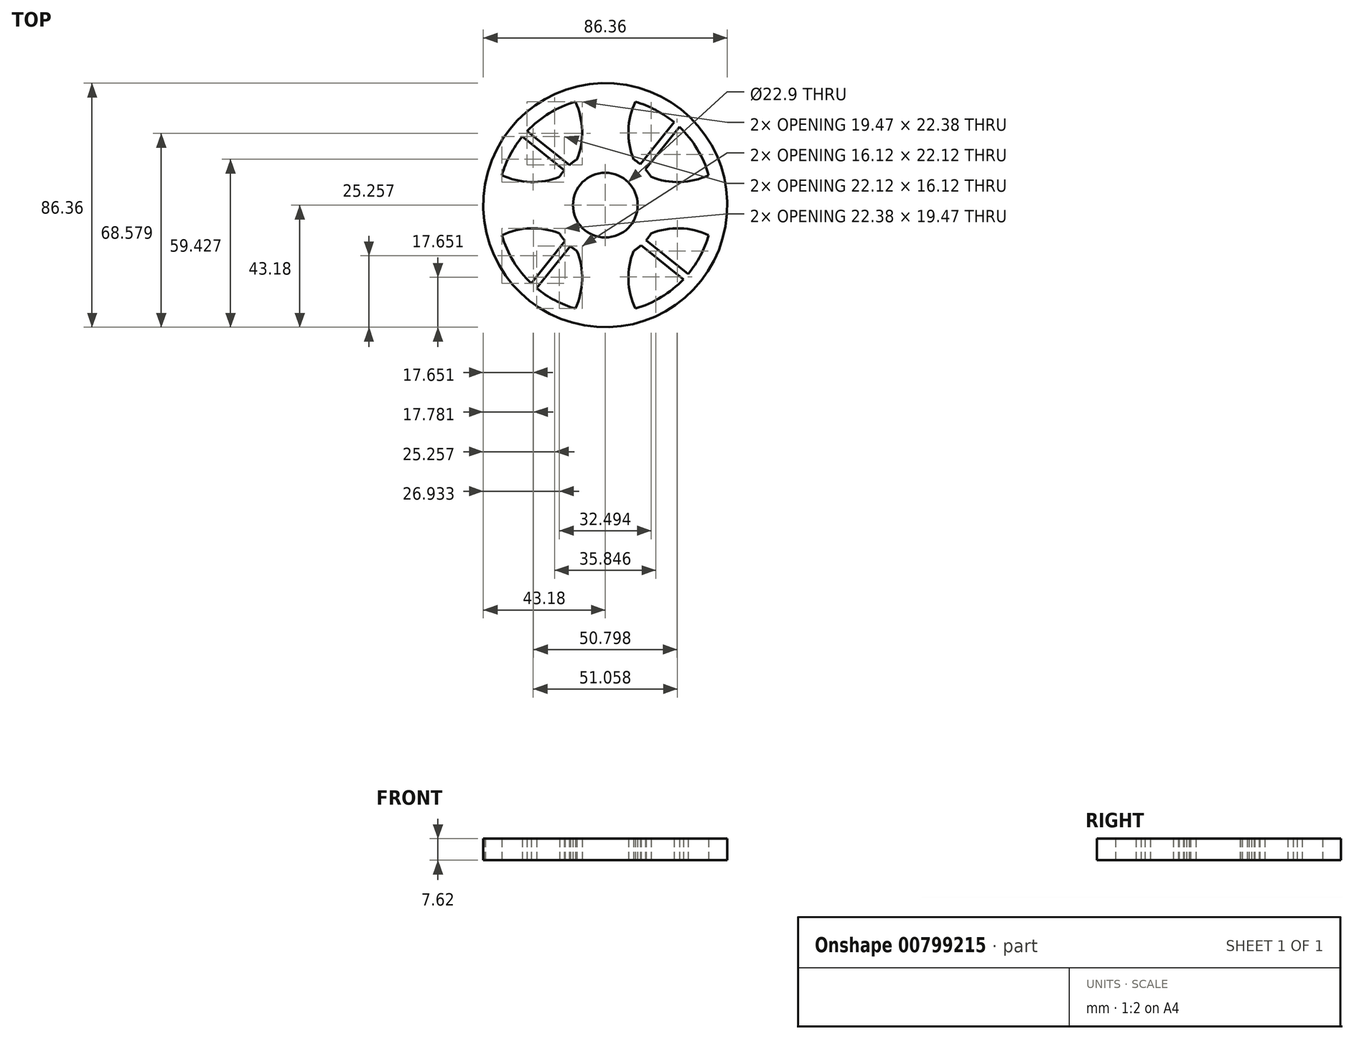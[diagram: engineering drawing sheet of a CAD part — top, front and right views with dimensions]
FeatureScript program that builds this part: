
annotation { "Feature Type Name" : "Feature", "Feature Type Description" : "" }
export const myFeature = defineFeature(function(context is Context, id is Id, definition is map)
    precondition{}
    {
        {
            var Q0;
            Q0=qCreatedBy(makeId("Top.planeOp"),FACE);
            var sketch = newSketch(context, id + "F0", { "sketchPlane" : qUnion([Q0])});
            skCircle(sketch, "E0", {"center": v(0, 0) * mm, "radius": 11.45 * mm});
            skCircle(sketch, "E1", {"center": v(0, 0) * mm, "radius": 19.05 * mm});
            skArc(sketch, "E2", {"start": v(-10.04, 16.2) * mm, "mid": v(-8.22, 27.23) * mm, "end": v(-11.33, 37.98) * mm});
            skArc(sketch, "E3.MirrorCS", {"start": v(10.04, 16.2) * mm, "mid": v(8.22, 27.23) * mm, "end": v(11.33, 37.98) * mm});
            skCircle(sketch, "E4", {"center": v(0, 0) * mm, "radius": 38.1 * mm});
            skCircle(sketch, "E5", {"center": v(0, 0) * mm, "radius": 43.18 * mm});
            skArc(sketch, "E6", {"start": v(0, 44.45) * mm, "mid": v(-6.68, 43) * mm, "end": v(-11.33, 37.98) * mm});
            skArc(sketch, "E7", {"start": v(11.33, 37.98) * mm, "mid": v(6.68, 43) * mm, "end": v(0, 44.45) * mm});
            skArc(sketch, "E8.1.1", {"start": v(-38.2, 11.02) * mm, "mid": v(-43.22, 6.37) * mm, "end": v(-44.68, -0.3) * mm});
            skArc(sketch, "E8.1.4", {"start": v(-44.45, 0) * mm, "mid": v(-43, -6.68) * mm, "end": v(-37.98, -11.33) * mm});
            skArc(sketch, "E8.1.6", {"start": v(-16.2, -10.04) * mm, "mid": v(-27.23, -8.22) * mm, "end": v(-37.98, -11.33) * mm});
            skArc(sketch, "E8.2.1", {"start": v(-11.33, -37.98) * mm, "mid": v(-6.68, -43) * mm, "end": v(0, -44.45) * mm});
            skArc(sketch, "E8.2.2", {"start": v(-10.04, -16.2) * mm, "mid": v(-8.22, -27.23) * mm, "end": v(-11.33, -37.98) * mm});
            skArc(sketch, "E8.2.4", {"start": v(0, -44.45) * mm, "mid": v(6.68, -43) * mm, "end": v(11.33, -37.98) * mm});
            skArc(sketch, "E8.2.6", {"start": v(10.04, -16.2) * mm, "mid": v(8.22, -27.23) * mm, "end": v(11.33, -37.98) * mm});
            skArc(sketch, "E8.3.1", {"start": v(37.98, -11.33) * mm, "mid": v(43, -6.68) * mm, "end": v(44.45, 0) * mm});
            skArc(sketch, "E8.3.2", {"start": v(16.2, -10.04) * mm, "mid": v(27.23, -8.22) * mm, "end": v(37.98, -11.33) * mm});
            skArc(sketch, "E8.3.4", {"start": v(44.45, 0) * mm, "mid": v(43, 6.68) * mm, "end": v(37.98, 11.33) * mm});
            skArc(sketch, "E8.3.6", {"start": v(16.2, 10.04) * mm, "mid": v(27.23, 8.22) * mm, "end": v(37.98, 11.33) * mm});
            skLineSegment(sketch, "E9", {"start": v(-14.47, 12.4) * mm, "end": v(-29.34, 24.3) * mm});
            skLineSegment(sketch, "E10", {"start": v(-12.69, 14.2) * mm, "end": v(-27.66, 26.2) * mm});
            skLineSegment(sketch, "E11.1.0", {"start": v(-12.4, -14.47) * mm, "end": v(-24.3, -29.34) * mm});
            skLineSegment(sketch, "E11.1.1", {"start": v(-14.2, -12.69) * mm, "end": v(-26.2, -27.66) * mm});
            skLineSegment(sketch, "E11.2.0", {"start": v(14.47, -12.4) * mm, "end": v(29.34, -24.3) * mm});
            skLineSegment(sketch, "E11.2.1", {"start": v(12.69, -14.2) * mm, "end": v(27.66, -26.2) * mm});
            skLineSegment(sketch, "E11.3.0", {"start": v(12.4, 14.47) * mm, "end": v(24.3, 29.34) * mm});
            skLineSegment(sketch, "E11.3.1", {"start": v(14.2, 12.69) * mm, "end": v(26.2, 27.66) * mm});
            skArc(sketch, "E12.MirrorCS", {"start": v(-16.2, 10.04) * mm, "mid": v(-27.23, 8.22) * mm, "end": v(-37.98, 11.33) * mm});
            skArc(sketch, "E13.MirrorCS", {"start": v(-44.45, 0) * mm, "mid": v(-43, 6.68) * mm, "end": v(-37.98, 11.33) * mm});
            skSolve(sketch);
        }
        {
            var Q0;
            {var subQ0=sQuery(id+"F0.wireOp",EDGE,"E2");var subQ1=sQuery(id+"F0.wireOp",EDGE,"E1");var subQ2=makeQuery(id+"F0.imprint","INTERSECT",VERTEX,{"derivedFrom":[subQ1,subQ0]});Q0=makeQuery(id+"F0.imprint","IMPRINT",FACE,{"disambiguationData":[TD([[makeQuery(id+"F0.imprint","IMPRINT",EDGE,{"disambiguationData":[TD([[subQ2,1.0]])],"derivedFrom":subQ1}),-1.0]])]});}
            var Q1;
            Q1=makeQuery(id+"F0.imprint","IMPRINT",FACE,{"disambiguationData":[TD([[makeQuery(id+"F0.imprint","IMPRINT",EDGE,{"derivedFrom":sQuery(id+"F0.wireOp",EDGE,"E0")}),-1.0]])]});
            var Q2;
            {var subQ1=sQuery(id+"F0.wireOp",EDGE,"E2");var subQ5=sQuery(id+"F0.wireOp",EDGE,"E6");var subQ6=makeQuery(id+"F0.imprint","INTERSECT",VERTEX,{"derivedFrom":[subQ1,subQ5]});Q2=makeQuery(id+"F0.imprint","IMPRINT",FACE,{"disambiguationData":[TD([[makeQuery(id+"F0.imprint","IMPRINT",EDGE,{"disambiguationData":[TD([[subQ6,1.0]])],"derivedFrom":subQ1}),-1.0]])]});}
            var Q3;
            {var subQ9=sQuery(id+"F0.wireOp",EDGE,"E2");var subQ11=sQuery(id+"F0.wireOp",EDGE,"E6");var subQ12=makeQuery(id+"F0.imprint","INTERSECT",VERTEX,{"derivedFrom":[subQ9,subQ11]});Q3=makeQuery(id+"F0.imprint","IMPRINT",FACE,{"disambiguationData":[TD([[makeQuery(id+"F0.imprint","IMPRINT",EDGE,{"disambiguationData":[TD([[subQ12,1.0]])],"derivedFrom":subQ9}),1.0]])]});}
            var Q4;
            {var subQ0=sQuery(id+"F0.wireOp",EDGE,"E8.1.2");var subQ5=sQuery(id+"F0.wireOp",EDGE,"E4");var subQ6=makeQuery(id+"F0.imprint","INTERSECT",VERTEX,{"derivedFrom":[subQ5,subQ0]});Q4=makeQuery(id+"F0.imprint","IMPRINT",FACE,{"disambiguationData":[TD([[makeQuery(id+"F0.imprint","IMPRINT",EDGE,{"disambiguationData":[TD([[subQ6,-1.0]])],"derivedFrom":subQ5}),-1.0]])]});}
            var Q5;
            {var subQ5=sQuery(id+"F0.wireOp",EDGE,"E4");var subQ7=makeQuery(id+"F0.imprint","INTERSECT",VERTEX,{"derivedFrom":[subQ5,sQuery(id+"F0.wireOp",EDGE,"E11.1.1")]});Q5=makeQuery(id+"F0.imprint","IMPRINT",FACE,{"disambiguationData":[TD([[makeQuery(id+"F0.imprint","IMPRINT",EDGE,{"disambiguationData":[TD([[subQ7,1.0]])],"derivedFrom":subQ5}),-1.0]])]});}
            var Q6;
            {var subQ0=sQuery(id+"F0.wireOp",EDGE,"E11.1.0");Q6=makeQuery(id+"F0.imprint","IMPRINT",FACE,{"disambiguationData":[TD([[makeQuery(id+"F0.imprint","IMPRINT",EDGE,{"derivedFrom":subQ0}),-1.0]])]});}
            var Q7;
            {var subQ0=sQuery(id+"F0.wireOp",EDGE,"E8.2.2");var subQ1=sQuery(id+"F0.wireOp",EDGE,"E1");var subQ2=makeQuery(id+"F0.imprint","INTERSECT",VERTEX,{"derivedFrom":[subQ1,subQ0]});Q7=makeQuery(id+"F0.imprint","IMPRINT",FACE,{"disambiguationData":[TD([[makeQuery(id+"F0.imprint","IMPRINT",EDGE,{"disambiguationData":[TD([[subQ2,-1.0]])],"derivedFrom":subQ1}),-1.0]])]});}
            var Q8;
            {var subQ0=sQuery(id+"F0.wireOp",EDGE,"E8.2.2");var subQ5=sQuery(id+"F0.wireOp",EDGE,"E4");var subQ6=makeQuery(id+"F0.imprint","INTERSECT",VERTEX,{"derivedFrom":[subQ5,subQ0]});Q8=makeQuery(id+"F0.imprint","IMPRINT",FACE,{"disambiguationData":[TD([[makeQuery(id+"F0.imprint","IMPRINT",EDGE,{"disambiguationData":[TD([[subQ6,-1.0]])],"derivedFrom":subQ5}),-1.0]])]});}
            var Q9;
            {var subQ3=sQuery(id+"F0.wireOp",EDGE,"E4");var subQ9=sQuery(id+"F0.wireOp",EDGE,"E8.3.6");var subQ10=makeQuery(id+"F0.imprint","INTERSECT",VERTEX,{"derivedFrom":[subQ3,subQ9]});Q9=makeQuery(id+"F0.imprint","IMPRINT",FACE,{"disambiguationData":[TD([[makeQuery(id+"F0.imprint","IMPRINT",EDGE,{"disambiguationData":[TD([[subQ10,1.0]])],"derivedFrom":subQ3}),-1.0]])]});}
            var Q10;
            {var subQ0=sQuery(id+"F0.wireOp",EDGE,"E8.3.2");var subQ1=sQuery(id+"F0.wireOp",EDGE,"E1");var subQ2=makeQuery(id+"F0.imprint","INTERSECT",VERTEX,{"derivedFrom":[subQ1,subQ0]});Q10=makeQuery(id+"F0.imprint","IMPRINT",FACE,{"disambiguationData":[TD([[makeQuery(id+"F0.imprint","IMPRINT",EDGE,{"disambiguationData":[TD([[subQ2,-1.0]])],"derivedFrom":subQ1}),-1.0]])]});}
            var Q11;
            {var subQ0=sQuery(id+"F0.wireOp",EDGE,"E11.2.0");Q11=makeQuery(id+"F0.imprint","IMPRINT",FACE,{"disambiguationData":[TD([[makeQuery(id+"F0.imprint","IMPRINT",EDGE,{"derivedFrom":subQ0}),-1.0]])]});}
            var Q12;
            {var subQ0=sQuery(id+"F0.wireOp",EDGE,"E9");Q12=makeQuery(id+"F0.imprint","IMPRINT",FACE,{"disambiguationData":[TD([[makeQuery(id+"F0.imprint","IMPRINT",EDGE,{"derivedFrom":subQ0}),-1.0]])]});}
            var Q13;
            {var subQ0=sQuery(id+"F0.wireOp",EDGE,"E11.3.0");Q13=makeQuery(id+"F0.imprint","IMPRINT",FACE,{"disambiguationData":[TD([[makeQuery(id+"F0.imprint","IMPRINT",EDGE,{"derivedFrom":subQ0}),-1.0]])]});}
            var Q14;
            {var subQ0=sQuery(id+"F0.wireOp",EDGE,"E4");var subQ4=makeQuery(id+"F0.imprint","INTERSECT",VERTEX,{"derivedFrom":[subQ0,sQuery(id+"F0.wireOp",EDGE,"E11.2.1")]});Q14=makeQuery(id+"F0.imprint","IMPRINT",FACE,{"disambiguationData":[TD([[makeQuery(id+"F0.imprint","IMPRINT",EDGE,{"disambiguationData":[TD([[subQ4,1.0]])],"derivedFrom":subQ0}),-1.0]])]});}
            var Q15;
            {var subQ2=sQuery(id+"F0.wireOp",EDGE,"E3.MirrorCS");var subQ11=sQuery(id+"F0.wireOp",EDGE,"E7");var subQ12=makeQuery(id+"F0.imprint","INTERSECT",VERTEX,{"derivedFrom":[subQ2,subQ11]});Q15=makeQuery(id+"F0.imprint","IMPRINT",FACE,{"disambiguationData":[TD([[makeQuery(id+"F0.imprint","IMPRINT",EDGE,{"disambiguationData":[TD([[subQ12,1.0]])],"derivedFrom":subQ2}),-1.0]])]});}
            var Q16;
            {var subQ0=sQuery(id+"F0.wireOp",EDGE,"KMxRPhfQ-wVzj-nbZw-Opsm-MwR3WpWLNZjw");var subQ9=sQuery(id+"F0.wireOp",EDGE,"E4");var subQ10=makeQuery(id+"F0.imprint","INTERSECT",VERTEX,{"derivedFrom":[subQ9,subQ0]});Q16=makeQuery(id+"F0.imprint","IMPRINT",FACE,{"disambiguationData":[TD([[makeQuery(id+"F0.imprint","IMPRINT",EDGE,{"disambiguationData":[TD([[subQ10,-1.0]])],"derivedFrom":subQ9}),-1.0]])]});}
            var Q17;
            {var subQ0=sQuery(id+"F0.wireOp",EDGE,"E8.1.6");var subQ1=sQuery(id+"F0.wireOp",EDGE,"E1");var subQ2=makeQuery(id+"F0.imprint","INTERSECT",VERTEX,{"derivedFrom":[subQ1,subQ0]});Q17=makeQuery(id+"F0.imprint","IMPRINT",FACE,{"disambiguationData":[TD([[makeQuery(id+"F0.imprint","IMPRINT",EDGE,{"disambiguationData":[TD([[subQ2,1.0]])],"derivedFrom":subQ1}),-1.0]])]});}
            var Q18;
            {var subQ3=sQuery(id+"F0.wireOp",EDGE,"E4");var subQ9=sQuery(id+"F0.wireOp",EDGE,"E12.MirrorCS");var subQ10=makeQuery(id+"F0.imprint","INTERSECT",VERTEX,{"derivedFrom":[subQ3,subQ9]});Q18=makeQuery(id+"F0.imprint","IMPRINT",FACE,{"disambiguationData":[TD([[makeQuery(id+"F0.imprint","IMPRINT",EDGE,{"disambiguationData":[TD([[subQ10,-1.0]])],"derivedFrom":subQ3}),-1.0]])]});}
            extrude(context, id + "F1", {"entities" : qUnion([Q0, Q1, Q2, Q3, Q4, Q5, Q6, Q7, Q8, Q9, Q10, Q11, Q12, Q13, Q14, Q15, Q16, Q17, Q18]), "depth" : 7.62 * mm, "offsetDistance" : 25.4 * mm});
        }
    });
